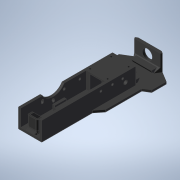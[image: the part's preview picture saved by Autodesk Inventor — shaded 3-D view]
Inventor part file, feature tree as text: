
AUTODESK INVENTOR PART (.ipt)
format: ipt  version: 2021 (Build 250183000, 183)  size: 492,032 bytes
history: native  units: mm
features: extrude x19, sketch x18, chamfer x5, mirror x2, fillet x1
ambient origin geometry x8: Origin, YZ Plane, XZ Plane, XY Plane, X Axis, Y Axis, Z Axis, Center Point
bodies: Body1 (feature_tree)
feature tree (45):
  extrude  "Extrusion27"  Depth=65.0mm
  extrude  "Extrusion28"  Depth=20.0mm
  extrude  "Extrusion29"  Depth=3.2mm
  extrude  "Extrusion33"  Depth=21.0mm
  chamfer  "Chamfer5"  Distance=28.25mm
  extrude  "Extrusion34"  Depth=3.0mm
  sketch  "Sketch35"  dims[d210=7.5mm]
  extrude  "Extrusion35"  Depth=23.0mm TaperAngle=0.0deg
  extrude  "Extrusion36"  Depth=16.2mm
  mirror  "Mirror1"
  extrude  "Extrusion42"  Depth=2.0mm
  extrude  "Extrusion44"  Depth=6.0mm TaperAngle=0.0deg
  extrude  "Extrusion45"  Depth=5.1mm
  chamfer  "Chamfer8"  Distance=6.0mm
  extrude  "Extrusion46"  Depth=1.0mm TaperAngle=0.0deg
  extrude  "Extrusion47"  Depth=6.0mm
  extrude  "Extrusion49"  Depth=6.0mm
  extrude  "Extrusion50"  Depth=6.0mm
  mirror  "Mirror3"
  extrude  "Extrusion53"  Depth=12.0mm
  extrude  "Extrusion60"  Depth=3.2mm
  extrude  "Extrusion61"  TaperAngle=0.0deg  [1 undecoded]
  extrude  "Extrusion54"  Depth=2.0mm
  extrude  "Extrusion62"  Depth=12.0mm
  chamfer  "Chamfer13"  Distance=24.0mm
  chamfer  "Chamfer14"  Distance=2.5mm
  chamfer  "Chamfer15"  Distance=31.5mm
  fillet  "Fillet6"  Radius=10.0mm
  sketch  "Sketch27"  dims[d198=32.0mm d199=65.0mm]
  sketch  "Sketch28"  dims[d200=40.0mm d201=20.0mm]
  sketch  "Sketch29"  dims[d204=3.0mm d205=0.0mm d206=3.2mm]
  sketch  "Sketch33"  dims[d207=15.0mm d208=21.0mm]
  sketch  "Sketch34"  dims[d209=8.0mm]
  sketch  "Sketch41"  dims[d211=5.0mm d212=28.25mm d213=0.0mm]
  sketch  "Sketch43"  dims[d215=3.0mm d217=3.0mm]
  sketch  "Sketch44"  dims[d218=3.0mm d219=23.0mm d220=0.0mm]
  sketch  "Sketch45"  dims[d234=45.2mm d235=16.2mm]
  sketch  "Sketch46"  dims[d236=6.0mm d237=0.0mm d238=2.0mm]
  sketch  "Sketch48"  dims[d239=1.85mm d240=2.0mm d241=45.0deg d245=6.0mm d246=0.0mm]
  sketch  "Sketch49"  dims[d247=13.5mm d248=5.1mm]
  sketch  "Sketch52"  dims[d249=25.0mm d250=6.0mm d251=0.0mm]
  sketch  "Sketch54"  dims[d252=5.5mm d253=1.0mm d254=0.0mm]
  sketch  "Sketch59"  dims[d255=21.0mm d285=6.0mm]
  sketch  "Sketch60"  dims[d286=3.2mm d287=6.0mm]
  sketch  "Sketch61"  dims[d288=12.0mm d296=6.0mm d297=12.0mm d298=3.2mm d300=0.0mm d301=0.0mm d314=2.8mm d315=12.0mm d316=24.0mm d317=2.5mm d318=31.5mm d319=10.0mm d320=0.0mm d321=3.0mm d322=3.0mm d323=10.0mm d324=0.0mm d325=13.0mm d326=14.0mm d327=10.0mm d328=0.0mm d329=3.2mm d331=10.0mm d332=20.0mm d333=14.0mm d334=0.0mm d335=0.0mm d342=8.0mm d343=50.0mm d344=10.0mm d345=10.0mm d346=0.0mm d347=2.8mm d348=6.0mm d350=7.0mm d351=0.0mm d352=14.0mm d353=18.0mm d354=16.0mm d355=3.5mm d356=6.0mm d357=2.0mm d358=45.0deg d370=2.8mm d371=5.0mm d372=7.0mm d373=0.0mm d375=35.0mm d376=9.0mm d377=4.0mm d378=0.0mm d412=23.0mm d413=12.0mm d414=16.0mm d416=12.75mm d417=0.0mm d418=6.1mm d419=2.85mm d420=0.0mm d424=11.0mm d425=22.0mm d427=22.0mm d430=15.0mm d431=3.2mm d432=22.0mm d433=22.0mm d434=2.0mm d435=39.5mm d436=45.5mm d437=72.5mm d438=92.5mm d439=10.0mm d440=32.0mm d441=2.0mm d442=10.0mm d443=2.0mm d444=17.0mm d445=0.0mm d446=2.0mm d447=2.0mm d448=45.0deg d449=17.0mm d450=2.0mm d451=45.0deg d452=2.0mm d453=3.0mm d454=2.0mm d455=45.0deg]
note: 1 required parameter value undecoded (feature->parameter linkage not recoverable at this tier; creation-order binding heuristic only, values carry confidence <= 0.55)
